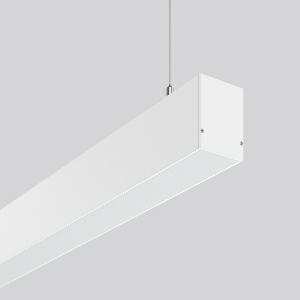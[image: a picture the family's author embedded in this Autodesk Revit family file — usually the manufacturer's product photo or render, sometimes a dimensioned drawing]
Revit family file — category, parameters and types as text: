
# Revit family: less_is_more_50_312314_002_76_edd6
name_source: partatom
category: Lighting Fixtures
units: mm (PartAtom-declared; Revit-internal decimal feet)

## family parameters
Cut with Voids When Loaded = No
Host = Face
Light Source = No
Part Type = Normal
Room Calculation Point = No
Round Connector Dimension = Use Diameter
Shared = No

## types (1)
- LESS IS MORE 50 (1 x LED Modul 830, 4650 lm, 3000)
    Apparent Load = 40 VA
    CIE Flux Codes = 48 79 95 100 100
    Color Rendering = 80
    Color Temperature = 3000
    Default Elevation = 1800 mm
    Description = Series: LESS IS MORE 50
Linear pendant luminaire for aesthetically sophisticated lighting. Housing: extruded aluminium profile, powder-coated. End cap aluminium powder-coated. Canopy made of aluminium, powder-coated. Diffuser made of non-yellowing plastic (PMMA), opal. Direct light emission. Suitable for pendant. 2-point steel cable suspension freely positionable and infinitely height-adjustable. Special lengths available on request. LED unit with integrated converter interchangeable and removable. Suitable for through-wiring. With sensors or as a safety luminaire on request. 
Colour: traffic white, matt (RAL 9016)
Length: 1687 mm
Width: 57 mm
Height: 75 mm
Suspension length: 2000 mm
Lamp: LED
Socket: without socket
Colour temperature: 3000K
Colour rendering index (CRI): 80
System power: 40 W
Rated luminous flux: 4650 lm
Luminous efficiency: 116 lm/W
Control gear: Converter, dimmable, DALI
Protection class: I
Type of protection: IP 20
    Height = 75 mm
    Lamp = 1 x LED Modul 830
    Lamp Light Flux = 4650 lm
    Lamp count = 1
    Length = 1687 mm
    Lifetime = 50000 h
    Luminous efficacy = 116 lm/W
    Manufacturer = RZB
    ModVariant = No
    Model = 312314.002.76
    Mounting Place = Ceiling
    Mounting Type = Pendant
    Number of Poles = 1
    OnlyDefault = Yes
    Power Factor = 1
    Product Name = LESS IS MORE 50
    Product group = Pendant LED linear luminaires
    ProductGroupID = 907
    Protection Class = Protection class I
    Protection Degree = IP 20
    RLX_Detail_Level = 1
    RLX_Emergency_Light_Flux = 0 lm
    RLX_Emergency_Type = 0
    RLX_Emergency_Type_DB = No
    RlxData = <blob elided: 20573 chars, md5=dd0fff37>
    Socket = socket
    Standby Power = 0 W
    System Light Flux = 4650 lm
    System Power = 40 W
    Type Comments = Product without accessories
    Type Image = 312318.002.jpg
    URL = http://relux.com
    VarID = ---
    Voltage = 230 V
    Voltage Range = 220-240 V
    Weight = 0.00 kg
    Width = 57 mm

## geometry (parser evidence)
native form markers: Blend x4, Sweep x13
no freeform markers — native parametric forms only
